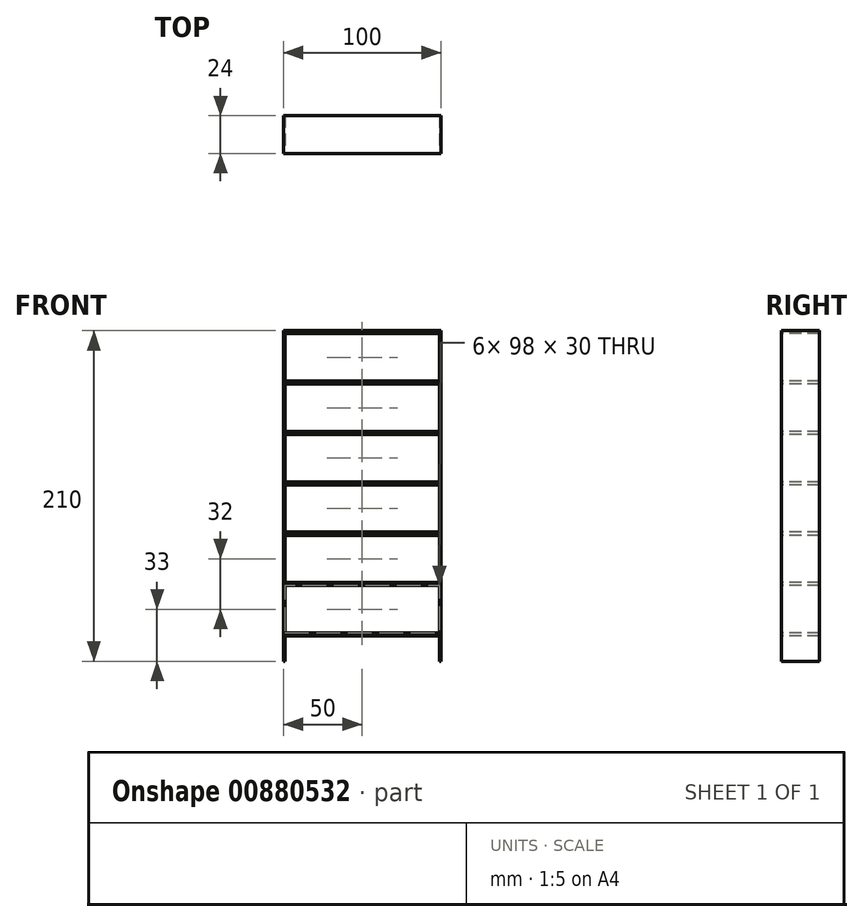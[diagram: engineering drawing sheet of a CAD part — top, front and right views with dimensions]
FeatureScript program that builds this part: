
annotation { "Feature Type Name" : "Feature", "Feature Type Description" : "" }
export const myFeature = defineFeature(function(context is Context, id is Id, definition is map)
    precondition{}
    {
        {
            var Q0;
            Q0=qCreatedBy(makeId("Top.planeOp"),FACE);
            var sketch = newSketch(context, id + "F0", { "sketchPlane" : qUnion([Q0])});
            skLineSegment(sketch, "E0.bottom", {"start": v(-220.04, -36.34) * mm, "end": v(-120.04, -36.34) * mm});
            skLineSegment(sketch, "E0.top", {"start": v(-220.04, -60.34) * mm, "end": v(-120.04, -60.34) * mm});
            skLineSegment(sketch, "E0.left", {"start": v(-220.04, -36.34) * mm, "end": v(-220.04, -60.34) * mm});
            skLineSegment(sketch, "E0.right", {"start": v(-120.04, -36.34) * mm, "end": v(-120.04, -60.34) * mm});
            skSolve(sketch);
        }
        {
            var Q0;
            Q0=makeQuery(id+"F0.imprint","IMPRINT",FACE,{"disambiguationData":[TD([[makeQuery(id+"F0.imprint","IMPRINT",EDGE,{"derivedFrom":sQuery(id+"F0.wireOp",EDGE,"E0.bottom")}),-1.0]])]});
            extrude(context, id + "F1", {"entities" : qUnion([Q0]), "oppositeDirection" : true, "depth" : 210 * mm, "offsetDistance" : 25 * mm});
        }
        {
            var Q0;
            Q0=makeQuery(id+"F1.opExtrude","SWEPT_FACE",FACE,{"disambiguationData":[OSD([sQuery(id+"F0.wireOp",EDGE,"E0.top")])]});
            var sketch = newSketch(context, id + "F2", { "sketchPlane" : qUnion([Q0])});
            skLineSegment(sketch, "E1.bottom", {"start": v(-121.04, -32) * mm, "end": v(-219.04, -32) * mm});
            skLineSegment(sketch, "E1.top", {"start": v(-121.04, -2) * mm, "end": v(-219.04, -2) * mm});
            skLineSegment(sketch, "E1.left", {"start": v(-121.04, -32) * mm, "end": v(-121.04, -2) * mm});
            skLineSegment(sketch, "E1.right", {"start": v(-219.04, -32) * mm, "end": v(-219.04, -2) * mm});
            skPoint(sketch, "E1.middle", {"position": v(-170.04, -17) * mm});
            skPoint(sketch, "E1.middle.positionSnap0", {"position": v(-170.04, 0) * mm});
            skPoint(sketch, "E1.centerSnap0", {"position": v(-170.04, 0) * mm});
            skLineSegment(sketch, "E2.bottom", {"start": v(-219.04, -34) * mm, "end": v(-121.04, -34) * mm});
            skLineSegment(sketch, "E2.top", {"start": v(-219.04, -64) * mm, "end": v(-121.04, -64) * mm});
            skLineSegment(sketch, "E2.left", {"start": v(-219.04, -34) * mm, "end": v(-219.04, -64) * mm});
            skLineSegment(sketch, "E2.right", {"start": v(-121.04, -34) * mm, "end": v(-121.04, -64) * mm});
            skLineSegment(sketch, "E3.bottom", {"start": v(-219.04, -66) * mm, "end": v(-121.04, -66) * mm});
            skLineSegment(sketch, "E3.top", {"start": v(-219.04, -96) * mm, "end": v(-121.04, -96) * mm});
            skLineSegment(sketch, "E3.left", {"start": v(-219.04, -66) * mm, "end": v(-219.04, -96) * mm});
            skLineSegment(sketch, "E3.right", {"start": v(-121.04, -66) * mm, "end": v(-121.04, -96) * mm});
            skLineSegment(sketch, "E4.bottom", {"start": v(-219.04, -98) * mm, "end": v(-121.04, -98) * mm});
            skLineSegment(sketch, "E4.top", {"start": v(-219.04, -128) * mm, "end": v(-121.04, -128) * mm});
            skLineSegment(sketch, "E4.left", {"start": v(-219.04, -98) * mm, "end": v(-219.04, -128) * mm});
            skLineSegment(sketch, "E4.right", {"start": v(-121.04, -98) * mm, "end": v(-121.04, -128) * mm});
            skLineSegment(sketch, "E5.bottom", {"start": v(-219.04, -130) * mm, "end": v(-121.04, -130) * mm});
            skLineSegment(sketch, "E5.top", {"start": v(-219.04, -160) * mm, "end": v(-121.04, -160) * mm});
            skLineSegment(sketch, "E5.left", {"start": v(-219.04, -130) * mm, "end": v(-219.04, -160) * mm});
            skLineSegment(sketch, "E5.right", {"start": v(-121.04, -130) * mm, "end": v(-121.04, -160) * mm});
            skLineSegment(sketch, "E6.bottom", {"start": v(-219.04, -162) * mm, "end": v(-121.04, -162) * mm});
            skLineSegment(sketch, "E6.top", {"start": v(-219.04, -192) * mm, "end": v(-121.04, -192) * mm});
            skLineSegment(sketch, "E6.left", {"start": v(-219.04, -162) * mm, "end": v(-219.04, -192) * mm});
            skLineSegment(sketch, "E6.right", {"start": v(-121.04, -162) * mm, "end": v(-121.04, -192) * mm});
            skLineSegment(sketch, "E7.bottom", {"start": v(-219.04, -194) * mm, "end": v(-121.04, -194) * mm});
            skLineSegment(sketch, "E7.top", {"start": v(-219.04, -210) * mm, "end": v(-121.04, -210) * mm});
            skLineSegment(sketch, "E7.left", {"start": v(-219.04, -194) * mm, "end": v(-219.04, -210) * mm});
            skLineSegment(sketch, "E7.right", {"start": v(-121.04, -194) * mm, "end": v(-121.04, -210) * mm});
            skSolve(sketch);
        }
        {
            var Q0;
            Q0=makeQuery(id+"F2.imprint","IMPRINT",FACE,{"disambiguationData":[TD([[makeQuery(id+"F2.imprint","IMPRINT",EDGE,{"derivedFrom":sQuery(id+"F2.wireOp",EDGE,"E1.bottom")}),-1.0]])]});
            var Q1;
            Q1=makeQuery(id+"F2.imprint","IMPRINT",FACE,{"disambiguationData":[TD([[makeQuery(id+"F2.imprint","IMPRINT",EDGE,{"derivedFrom":sQuery(id+"F2.wireOp",EDGE,"E2.bottom")}),-1.0]])]});
            var Q2;
            Q2=makeQuery(id+"F2.imprint","IMPRINT",FACE,{"disambiguationData":[TD([[makeQuery(id+"F2.imprint","IMPRINT",EDGE,{"derivedFrom":sQuery(id+"F2.wireOp",EDGE,"E3.bottom")}),-1.0]])]});
            var Q3;
            Q3=makeQuery(id+"F2.imprint","IMPRINT",FACE,{"disambiguationData":[TD([[makeQuery(id+"F2.imprint","IMPRINT",EDGE,{"derivedFrom":sQuery(id+"F2.wireOp",EDGE,"E4.bottom")}),-1.0]])]});
            var Q4;
            Q4=makeQuery(id+"F2.imprint","IMPRINT",FACE,{"disambiguationData":[TD([[makeQuery(id+"F2.imprint","IMPRINT",EDGE,{"derivedFrom":sQuery(id+"F2.wireOp",EDGE,"E5.bottom")}),-1.0]])]});
            var Q5;
            Q5=makeQuery(id+"F2.imprint","IMPRINT",FACE,{"disambiguationData":[TD([[makeQuery(id+"F2.imprint","IMPRINT",EDGE,{"derivedFrom":sQuery(id+"F2.wireOp",EDGE,"E6.bottom")}),-1.0]])]});
            var Q6;
            Q6=makeQuery(id+"F2.imprint","IMPRINT",FACE,{"disambiguationData":[TD([[makeQuery(id+"F2.imprint","IMPRINT",EDGE,{"derivedFrom":sQuery(id+"F2.wireOp",EDGE,"E7.bottom")}),-1.0]])]});
            extrude(context, id + "F3", {"entities" : qUnion([Q0, Q1, Q2, Q3, Q4, Q5, Q6]), "operationType" : NewBodyOperationType.REMOVE, "oppositeDirection" : true, "depth" : 26 * mm, "offsetDistance" : 25 * mm});
        }
    });
